# Revit family: 1429xxx Tacoma_Single_UL
name_source: partatom
category: Lighting Fixtures
units: mm (PartAtom-declared; Revit-internal decimal feet)

## family parameters
Always vertical = Yes
Cut with Voids When Loaded = No
Host = Wall
Light Source = No
OmniClass Number = 23.80.70.00
OmniClass Title = Lighting
Part Type = Normal
Room Calculation Point = No
Round Connector Dimension = Use Diameter
Shared = No

## types (3) — shared parameters
ADA compliant = Yes
Acessories = Glass Shade options (Seperate item) : Smooth Opal , Ribbed Opal, Ribbed Smoke
Dimmable = Yes
Dimming Method = Lamp Dependent
Driver Included = Not Applicable
Driver Required = No
Efficacy (lm/w) = Lamp Dependent
Electrical Class = 1
Lamp = G9 LED
Length of Cable Supplied = 6 inch flying leads
Light Source Fixed = No
Location / IP Rating = Damp
Main Material = Metal - Mild Steel / Zinc
Manufacturer = Astro Lighting Ltd
Manufacturer URL - Europe and Rest of World = www.astrolighting.com
Manufacturer URL - North America = us.astrolighting.com
Power (Watts) = Lamp Dependent
Product CCT = Lamp Dependent
Product CRI = Lamp Dependent
Product Dimensions (Inch) = H 10.63 x W 4.33 x D 4.92
Product Location = Interior
Product URL = https://us.astrolighting.com
Product Weight (LB) = 2.32
URL = www.astrolighting.com
Wattage Comments = 3.5 W max
zero-valued in all types: Default Elevation

## per-type parameters (varying)
| type | Main Finish | Product Name | Product SKU |
| Astro_Tacoma_Single_Matt Black | Matt Black | Tacoma Single Matt Black | 1429013 |
| Astro_Tacoma_Single_Polished Chrome | Polished Chrome | Tacoma Single Polished Chrome | 1429010 |
| Astro_Tacoma_Single_Antique Brass | Antique Brass | Tacoma Single Polished Chrome | 1429016 |

## geometry (parser evidence)
native form markers: Sweep x2
no freeform markers — native parametric forms only
